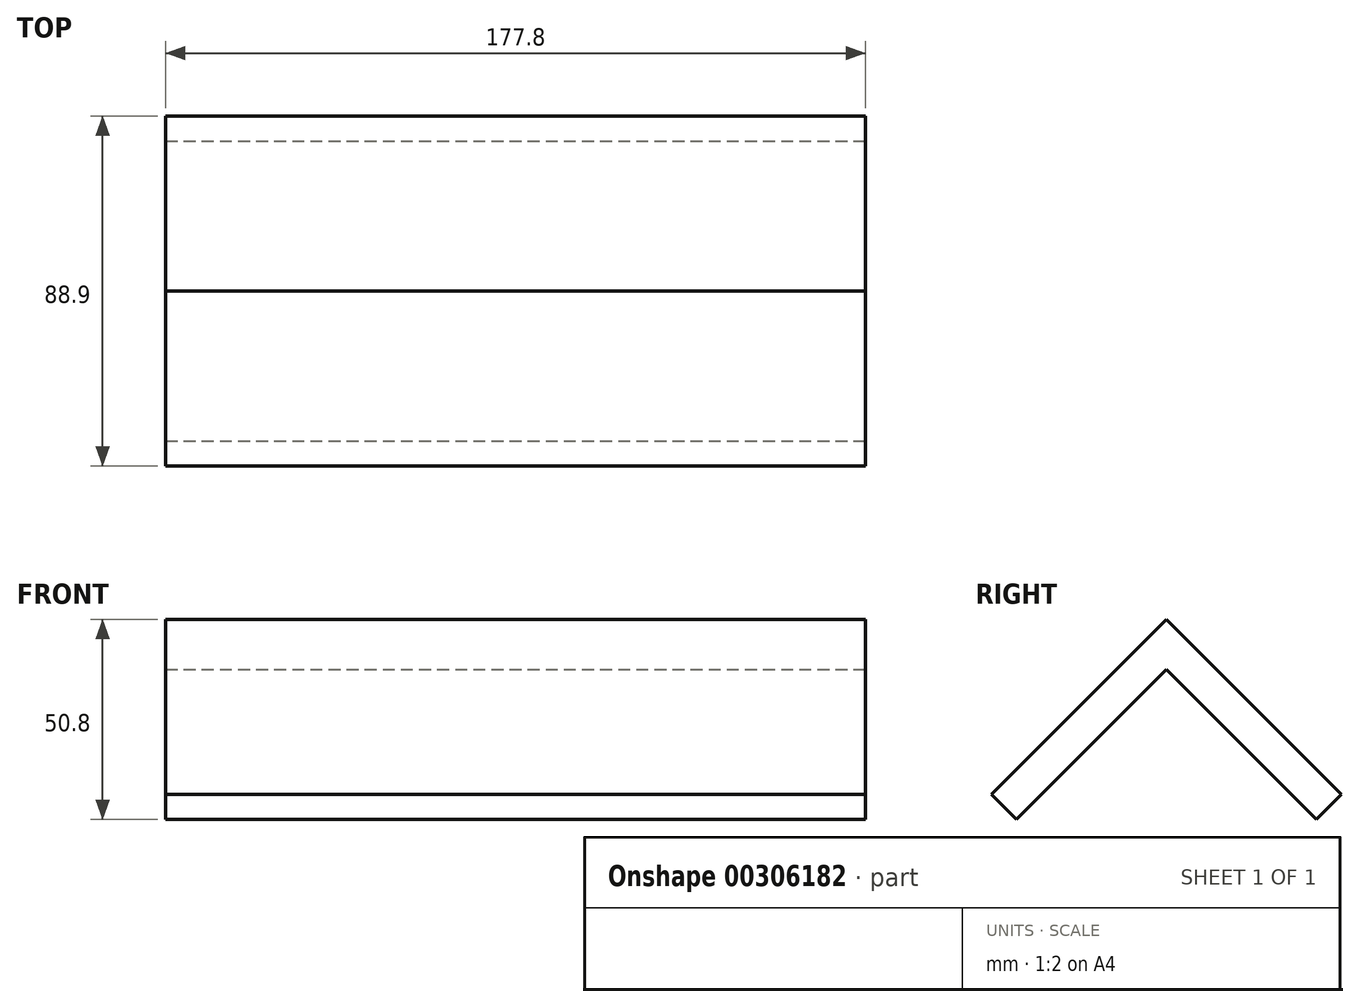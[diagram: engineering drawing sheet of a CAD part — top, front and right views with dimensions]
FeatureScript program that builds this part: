
annotation { "Feature Type Name" : "Feature", "Feature Type Description" : "" }
export const myFeature = defineFeature(function(context is Context, id is Id, definition is map)
    precondition{}
    {
        {
            var Q0;
            Q0=qCreatedBy(makeId("Front.planeOp"),FACE);
            var sketch = newSketch(context, id + "F0", { "sketchPlane" : qUnion([Q0])});
            skLineSegment(sketch, "E0.bottom", {"start": v(6.35, -25.4) * mm, "end": v(-6.35, -25.4) * mm});
            skLineSegment(sketch, "E0.top", {"start": v(6.35, 25.4) * mm, "end": v(-6.35, 25.4) * mm});
            skLineSegment(sketch, "E0.left", {"start": v(6.35, -25.4) * mm, "end": v(6.35, 25.4) * mm});
            skLineSegment(sketch, "E0.right", {"start": v(-6.35, -25.4) * mm, "end": v(-6.35, 25.4) * mm});
            skPoint(sketch, "E0.middle", {"position": v(0, 0) * mm});
            skSolve(sketch);
        }
        {
            var Q0;
            Q0=makeQuery(id+"F0.imprint","IMPRINT",FACE,{"disambiguationData":[TD([[makeQuery(id+"F0.imprint","IMPRINT",EDGE,{"derivedFrom":sQuery(id+"F0.wireOp",EDGE,"E0.bottom")}),-1.0]])]});
            extrude(context, id + "F1", {"entities" : qUnion([Q0]), "depth" : 101.6 * mm});
        }
        {
            var Q0;
            Q0=makeQuery(id+"F1.opExtrude","SWEPT_FACE",FACE,{"disambiguationData":[OSD([sQuery(id+"F0.wireOp",EDGE,"E0.left")])]});
            var sketch = newSketch(context, id + "F2", { "sketchPlane" : qUnion([Q0])});
            skLineSegment(sketch, "E1", {"start": v(-101.6, -25.4) * mm, "end": v(-50.8, 25.4) * mm});
            skLineSegment(sketch, "E2", {"start": v(-50.8, 25.4) * mm, "end": v(0, -25.4) * mm});
            skLineSegment(sketch, "E3", {"start": v(-101.6, -25.4) * mm, "end": v(0, -25.4) * mm});
            skSolve(sketch);
        }
        {
            var Q0;
            {var subQ0=sQuery(id+"F2.wireOp",EDGE,"E1");Q0=makeQuery(id+"F2.imprint","IMPRINT",FACE,{"disambiguationData":[TD([[makeQuery(id+"F2.imprint","IMPRINT",EDGE,{"derivedFrom":subQ0}),1.0]])]});}
            var Q1;
            {var subQ0=sQuery(id+"F2.wireOp",EDGE,"E2");Q1=makeQuery(id+"F2.imprint","IMPRINT",FACE,{"disambiguationData":[TD([[makeQuery(id+"F2.imprint","IMPRINT",EDGE,{"derivedFrom":subQ0}),1.0]])]});}
            extrude(context, id + "F3", {"entities" : qUnion([Q0, Q1]), "operationType" : NewBodyOperationType.REMOVE, "endBound" : BoundingType.THROUGH_ALL, "oppositeDirection" : true, "depth" : 25.4 * mm});
        }
        {
            var Q0;
            Q0=makeQuery(id+"F1.opExtrude","SWEPT_FACE",FACE,{"disambiguationData":[OSD([sQuery(id+"F0.wireOp",EDGE,"E0.right")])]});
            extrude(context, id + "F4", {"entities" : qUnion([Q0]), "operationType" : NewBodyOperationType.ADD, "depth" : 165.1 * mm});
        }
        {
            var Q0;
            Q0=makeQuery(id+"F1.opExtrude","SWEPT_FACE",FACE,{"disambiguationData":[OSD([sQuery(id+"F0.wireOp",EDGE,"E0.left")])]});
            var sketch = newSketch(context, id + "F5", { "sketchPlane" : qUnion([Q0])});
            skLineSegment(sketch, "E4", {"start": v(-101.6, -25.4) * mm, "end": v(-88.9, -25.4) * mm});
            skLineSegment(sketch, "E5", {"start": v(0, -25.4) * mm, "end": v(-12.7, -25.4) * mm});
            skLineSegment(sketch, "E6", {"start": v(-88.9, -25.4) * mm, "end": v(-44.45, 19.05) * mm});
            skLineSegment(sketch, "E7", {"start": v(-12.7, -25.4) * mm, "end": v(-57.15, 19.05) * mm});
            skLineSegment(sketch, "E8", {"start": v(-50.8, 25.4) * mm, "end": v(-44.45, 19.05) * mm});
            skSolve(sketch);
        }
        {
            var Q0;
            {var subQ0=sQuery(id+"F5.wireOp",EDGE,"E6");var subQ3=sQuery(id+"F5.wireOp",EDGE,"E7");var subQ4=makeQuery(id+"F5.imprint","INTERSECT",VERTEX,{"derivedFrom":[subQ0,subQ3]});Q0=makeQuery(id+"F5.imprint","IMPRINT",FACE,{"disambiguationData":[TD([[makeQuery(id+"F5.imprint","IMPRINT",EDGE,{"disambiguationData":[TD([[subQ4,1.0]])],"derivedFrom":subQ0}),-1.0]])]});}
            extrude(context, id + "F6", {"entities" : qUnion([Q0]), "operationType" : NewBodyOperationType.REMOVE, "endBound" : BoundingType.THROUGH_ALL, "oppositeDirection" : true, "depth" : 25.4 * mm});
        }
        {
            var Q0;
            Q0=makeQuery(id+"F1.opExtrude","SWEPT_FACE",FACE,{"disambiguationData":[OSD([sQuery(id+"F0.wireOp",EDGE,"E0.left")])]});
            var sketch = newSketch(context, id + "F7", { "sketchPlane" : qUnion([Q0])});
            skLineSegment(sketch, "E9", {"start": v(-88.9, -25.4) * mm, "end": v(-95.25, -19.05) * mm});
            skLineSegment(sketch, "E10", {"start": v(-95.25, -19.05) * mm, "end": v(-101.6, -25.4) * mm});
            skLineSegment(sketch, "E11", {"start": v(-101.6, -25.4) * mm, "end": v(-88.9, -25.4) * mm});
            skLineSegment(sketch, "E12", {"start": v(-12.7, -25.4) * mm, "end": v(-6.35, -19.05) * mm});
            skLineSegment(sketch, "E13", {"start": v(-6.35, -19.05) * mm, "end": v(0, -25.4) * mm});
            skLineSegment(sketch, "E14", {"start": v(0, -25.4) * mm, "end": v(-12.7, -25.4) * mm});
            skSolve(sketch);
        }
        {
            var Q0;
            Q0=makeQuery(id+"F7.imprint","IMPRINT",FACE,{"disambiguationData":[TD([[makeQuery(id+"F7.imprint","IMPRINT",EDGE,{"derivedFrom":sQuery(id+"F7.wireOp",EDGE,"E12")}),-1.0]])]});
            var Q1;
            Q1=makeQuery(id+"F7.imprint","IMPRINT",FACE,{"disambiguationData":[TD([[makeQuery(id+"F7.imprint","IMPRINT",EDGE,{"derivedFrom":sQuery(id+"F7.wireOp",EDGE,"E9")}),1.0]])]});
            extrude(context, id + "F8", {"entities" : qUnion([Q0, Q1]), "operationType" : NewBodyOperationType.REMOVE, "endBound" : BoundingType.THROUGH_ALL, "oppositeDirection" : true, "depth" : 25.4 * mm});
        }
    });
